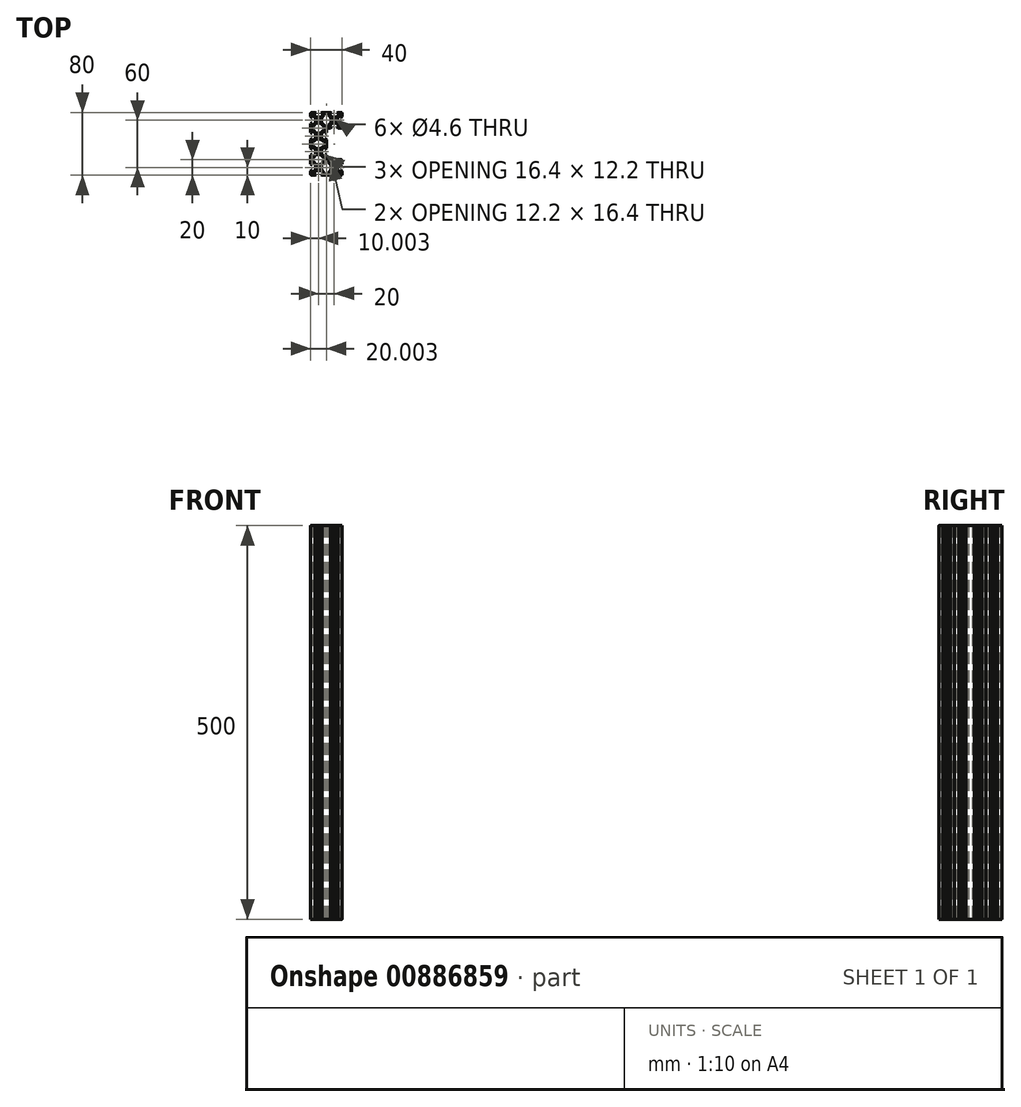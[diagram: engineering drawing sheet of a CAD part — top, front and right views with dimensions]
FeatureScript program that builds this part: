
annotation { "Feature Type Name" : "Feature", "Feature Type Description" : "" }
export const myFeature = defineFeature(function(context is Context, id is Id, definition is map)
    precondition{}
    {
        {
            var Q0;
            Q0=qCreatedBy(makeId("Top.planeOp"),FACE);
            var sketch = newSketch(context, id + "F0", { "sketchPlane" : qUnion([Q0])});
            skLineSegment(sketch, "E0", {"start": v(-12.56, -40) * mm, "end": v(-11.37, -38.82) * mm});
            skLineSegment(sketch, "E1", {"start": v(-11.37, -38.82) * mm, "end": v(-11.37, -38.2) * mm});
            skLineSegment(sketch, "E2", {"start": v(-11.37, -38.2) * mm, "end": v(-13.48, -38.2) * mm});
            skLineSegment(sketch, "E3", {"start": v(-13.48, -38.2) * mm, "end": v(-13.48, -36.56) * mm});
            skLineSegment(sketch, "E4", {"start": v(-13.48, -36.56) * mm, "end": v(-10.82, -33.9) * mm});
            skLineSegment(sketch, "E5", {"start": v(-10.82, -33.9) * mm, "end": v(-8.19, -33.9) * mm});
            skLineSegment(sketch, "E6", {"start": v(-8.19, -33.9) * mm, "end": v(-7.98, -33.7) * mm});
            skLineSegment(sketch, "E7", {"start": v(-7.98, -33.69) * mm, "end": v(-7.77, -33.9) * mm});
            skLineSegment(sketch, "E8", {"start": v(-7.77, -33.9) * mm, "end": v(-5.14, -33.9) * mm});
            skLineSegment(sketch, "E9", {"start": v(-5.14, -33.9) * mm, "end": v(-2.48, -36.56) * mm});
            skLineSegment(sketch, "E10", {"start": v(-2.48, -36.56) * mm, "end": v(-2.48, -38.2) * mm});
            skLineSegment(sketch, "E11", {"start": v(-2.48, -38.2) * mm, "end": v(-4.58, -38.2) * mm});
            skLineSegment(sketch, "E12", {"start": v(-4.58, -38.2) * mm, "end": v(-4.58, -38.82) * mm});
            skLineSegment(sketch, "E13", {"start": v(-4.58, -38.82) * mm, "end": v(-3.4, -40) * mm});
            skLineSegment(sketch, "E14", {"start": v(-3.4, -40) * mm, "end": v(7.44, -40) * mm});
            skLineSegment(sketch, "E15", {"start": v(7.44, -40) * mm, "end": v(8.63, -38.82) * mm});
            skLineSegment(sketch, "E16", {"start": v(8.63, -38.82) * mm, "end": v(8.63, -38.2) * mm});
            skLineSegment(sketch, "E17", {"start": v(8.63, -38.2) * mm, "end": v(6.52, -38.2) * mm});
            skLineSegment(sketch, "E18", {"start": v(6.52, -38.2) * mm, "end": v(6.52, -36.56) * mm});
            skLineSegment(sketch, "E19", {"start": v(6.52, -36.56) * mm, "end": v(9.18, -33.9) * mm});
            skLineSegment(sketch, "E20", {"start": v(9.18, -33.9) * mm, "end": v(11.81, -33.9) * mm});
            skLineSegment(sketch, "E21", {"start": v(11.81, -33.9) * mm, "end": v(12.02, -33.69) * mm});
            skLineSegment(sketch, "E22", {"start": v(12.02, -33.7) * mm, "end": v(12.23, -33.9) * mm});
            skLineSegment(sketch, "E23", {"start": v(12.23, -33.9) * mm, "end": v(14.86, -33.9) * mm});
            skLineSegment(sketch, "E24", {"start": v(14.86, -33.9) * mm, "end": v(17.52, -36.56) * mm});
            skLineSegment(sketch, "E25", {"start": v(17.52, -36.56) * mm, "end": v(17.52, -38.2) * mm});
            skLineSegment(sketch, "E26", {"start": v(17.52, -38.2) * mm, "end": v(15.42, -38.2) * mm});
            skLineSegment(sketch, "E27", {"start": v(15.42, -38.2) * mm, "end": v(15.42, -38.82) * mm});
            skLineSegment(sketch, "E28", {"start": v(15.42, -38.82) * mm, "end": v(16.6, -40) * mm});
            skLineSegment(sketch, "E29", {"start": v(16.6, -40) * mm, "end": v(20.52, -40) * mm});
            skLineSegment(sketch, "E30", {"start": v(22.02, -38.5) * mm, "end": v(22.02, -34.58) * mm});
            skLineSegment(sketch, "E31", {"start": v(22.02, -34.58) * mm, "end": v(20.84, -33.4) * mm});
            skLineSegment(sketch, "E32", {"start": v(20.84, -33.4) * mm, "end": v(20.22, -33.4) * mm});
            skLineSegment(sketch, "E33", {"start": v(20.22, -33.4) * mm, "end": v(20.22, -35.5) * mm});
            skLineSegment(sketch, "E34", {"start": v(20.22, -35.5) * mm, "end": v(18.58, -35.5) * mm});
            skLineSegment(sketch, "E35", {"start": v(18.58, -35.5) * mm, "end": v(15.92, -32.84) * mm});
            skLineSegment(sketch, "E36", {"start": v(15.92, -32.84) * mm, "end": v(15.92, -30.21) * mm});
            skLineSegment(sketch, "E37", {"start": v(15.92, -30.21) * mm, "end": v(15.71, -30) * mm});
            skLineSegment(sketch, "E38", {"start": v(15.71, -30) * mm, "end": v(15.92, -29.79) * mm});
            skLineSegment(sketch, "E39", {"start": v(15.92, -29.79) * mm, "end": v(15.92, -27.16) * mm});
            skLineSegment(sketch, "E40", {"start": v(15.92, -27.16) * mm, "end": v(18.58, -24.5) * mm});
            skLineSegment(sketch, "E41", {"start": v(18.58, -24.5) * mm, "end": v(20.22, -24.5) * mm});
            skLineSegment(sketch, "E42", {"start": v(20.22, -24.5) * mm, "end": v(20.22, -26.6) * mm});
            skLineSegment(sketch, "E43", {"start": v(20.22, -26.6) * mm, "end": v(20.84, -26.6) * mm});
            skLineSegment(sketch, "E44", {"start": v(20.84, -26.6) * mm, "end": v(22.02, -25.42) * mm});
            skLineSegment(sketch, "E45", {"start": v(22.02, -25.42) * mm, "end": v(22.02, -21.5) * mm});
            skLineSegment(sketch, "E46", {"start": v(20.52, -20) * mm, "end": v(16.6, -20) * mm});
            skLineSegment(sketch, "E47", {"start": v(16.6, -20) * mm, "end": v(15.42, -21.18) * mm});
            skLineSegment(sketch, "E48", {"start": v(15.42, -21.18) * mm, "end": v(15.42, -21.8) * mm});
            skLineSegment(sketch, "E49", {"start": v(15.42, -21.8) * mm, "end": v(17.52, -21.8) * mm});
            skLineSegment(sketch, "E50", {"start": v(17.52, -21.8) * mm, "end": v(17.52, -23.44) * mm});
            skLineSegment(sketch, "E51", {"start": v(17.52, -23.44) * mm, "end": v(14.86, -26.1) * mm});
            skLineSegment(sketch, "E52", {"start": v(14.86, -26.1) * mm, "end": v(12.23, -26.1) * mm});
            skLineSegment(sketch, "E53", {"start": v(12.23, -26.1) * mm, "end": v(12.02, -26.3) * mm});
            skLineSegment(sketch, "E54", {"start": v(12.02, -26.3) * mm, "end": v(11.81, -26.1) * mm});
            skLineSegment(sketch, "E55", {"start": v(11.81, -26.1) * mm, "end": v(9.18, -26.1) * mm});
            skLineSegment(sketch, "E56", {"start": v(9.18, -26.1) * mm, "end": v(6.52, -23.44) * mm});
            skLineSegment(sketch, "E57", {"start": v(6.52, -23.44) * mm, "end": v(6.52, -21.8) * mm});
            skLineSegment(sketch, "E58", {"start": v(-12.56, -40) * mm, "end": v(-16.48, -40) * mm});
            skLineSegment(sketch, "E59", {"start": v(6.52, -21.8) * mm, "end": v(8.63, -21.8) * mm});
            skLineSegment(sketch, "E60", {"start": v(-17.98, -38.5) * mm, "end": v(-17.98, -34.58) * mm});
            skLineSegment(sketch, "E61", {"start": v(8.63, -21.8) * mm, "end": v(8.63, -21.18) * mm});
            skLineSegment(sketch, "E62", {"start": v(-17.98, -34.58) * mm, "end": v(-16.8, -33.4) * mm});
            skLineSegment(sketch, "E63", {"start": v(8.63, -21.18) * mm, "end": v(7.44, -20) * mm});
            skLineSegment(sketch, "E64", {"start": v(-16.8, -33.4) * mm, "end": v(-16.18, -33.4) * mm});
            skLineSegment(sketch, "E65", {"start": v(7.44, -20) * mm, "end": v(2.02, -20) * mm});
            skLineSegment(sketch, "E66", {"start": v(-16.18, -33.4) * mm, "end": v(-16.18, -35.5) * mm});
            skLineSegment(sketch, "E67", {"start": v(2.02, -20) * mm, "end": v(2.02, -14.58) * mm});
            skLineSegment(sketch, "E68", {"start": v(-16.18, -35.5) * mm, "end": v(-14.54, -35.5) * mm});
            skLineSegment(sketch, "E69", {"start": v(2.02, -14.58) * mm, "end": v(0.84, -13.4) * mm});
            skLineSegment(sketch, "E70", {"start": v(-14.54, -35.5) * mm, "end": v(-11.88, -32.84) * mm});
            skLineSegment(sketch, "E71", {"start": v(0.84, -13.4) * mm, "end": v(0.22, -13.4) * mm});
            skLineSegment(sketch, "E72", {"start": v(-11.88, -32.84) * mm, "end": v(-11.88, -30.21) * mm});
            skLineSegment(sketch, "E73", {"start": v(0.22, -13.4) * mm, "end": v(0.22, -15.5) * mm});
            skLineSegment(sketch, "E74", {"start": v(-11.88, -30.21) * mm, "end": v(-11.67, -30) * mm});
            skLineSegment(sketch, "E75", {"start": v(0.22, -15.5) * mm, "end": v(-1.42, -15.5) * mm});
            skLineSegment(sketch, "E76", {"start": v(-11.67, -30) * mm, "end": v(-11.88, -29.79) * mm});
            skLineSegment(sketch, "E77", {"start": v(-1.42, -15.5) * mm, "end": v(-4.08, -12.84) * mm});
            skLineSegment(sketch, "E78", {"start": v(-11.88, -29.79) * mm, "end": v(-11.88, -27.16) * mm});
            skLineSegment(sketch, "E79", {"start": v(-4.08, -12.84) * mm, "end": v(-4.08, -10.21) * mm});
            skLineSegment(sketch, "E80", {"start": v(-11.88, -27.16) * mm, "end": v(-14.54, -24.5) * mm});
            skLineSegment(sketch, "E81", {"start": v(-4.08, -10.21) * mm, "end": v(-4.29, -10) * mm});
            skLineSegment(sketch, "E82", {"start": v(-14.54, -24.5) * mm, "end": v(-16.18, -24.5) * mm});
            skLineSegment(sketch, "E83", {"start": v(-4.29, -10) * mm, "end": v(-4.08, -9.8) * mm});
            skLineSegment(sketch, "E84", {"start": v(-16.18, -24.5) * mm, "end": v(-16.18, -26.6) * mm});
            skLineSegment(sketch, "E85", {"start": v(-4.08, -9.8) * mm, "end": v(-4.08, -7.16) * mm});
            skLineSegment(sketch, "E86", {"start": v(-16.18, -26.6) * mm, "end": v(-16.8, -26.6) * mm});
            skLineSegment(sketch, "E87", {"start": v(-4.08, -7.16) * mm, "end": v(-1.42, -4.5) * mm});
            skLineSegment(sketch, "E88", {"start": v(-16.8, -26.6) * mm, "end": v(-17.98, -25.42) * mm});
            skLineSegment(sketch, "E89", {"start": v(-1.42, -4.5) * mm, "end": v(0.22, -4.5) * mm});
            skLineSegment(sketch, "E90", {"start": v(-17.98, -25.42) * mm, "end": v(-17.98, -14.58) * mm});
            skLineSegment(sketch, "E91", {"start": v(0.22, -4.5) * mm, "end": v(0.22, -6.6) * mm});
            skLineSegment(sketch, "E92", {"start": v(-17.98, -14.58) * mm, "end": v(-16.8, -13.4) * mm});
            skLineSegment(sketch, "E93", {"start": v(0.22, -6.6) * mm, "end": v(0.84, -6.6) * mm});
            skLineSegment(sketch, "E94", {"start": v(-16.8, -13.4) * mm, "end": v(-16.18, -13.4) * mm});
            skLineSegment(sketch, "E95", {"start": v(0.84, -6.6) * mm, "end": v(2.02, -5.42) * mm});
            skLineSegment(sketch, "E96", {"start": v(-16.18, -13.4) * mm, "end": v(-16.18, -15.5) * mm});
            skLineSegment(sketch, "E97", {"start": v(2.02, -5.42) * mm, "end": v(2.02, 0) * mm});
            skLineSegment(sketch, "E98", {"start": v(-16.18, -15.5) * mm, "end": v(-14.54, -15.5) * mm});
            skLineSegment(sketch, "E99", {"start": v(-14.54, -15.5) * mm, "end": v(-11.88, -12.84) * mm});
            skLineSegment(sketch, "E100", {"start": v(-11.88, -12.84) * mm, "end": v(-11.88, -10.21) * mm});
            skLineSegment(sketch, "E101", {"start": v(-11.88, -10.21) * mm, "end": v(-11.67, -10) * mm});
            skLineSegment(sketch, "E102", {"start": v(-11.67, -10) * mm, "end": v(-11.88, -9.8) * mm});
            skLineSegment(sketch, "E103", {"start": v(-11.88, -9.8) * mm, "end": v(-11.88, -7.16) * mm});
            skLineSegment(sketch, "E104", {"start": v(-11.88, -7.16) * mm, "end": v(-14.54, -4.5) * mm});
            skLineSegment(sketch, "E105", {"start": v(-14.54, -4.5) * mm, "end": v(-16.18, -4.5) * mm});
            skLineSegment(sketch, "E106", {"start": v(-16.18, -4.5) * mm, "end": v(-16.18, -6.6) * mm});
            skLineSegment(sketch, "E107", {"start": v(-16.18, -6.6) * mm, "end": v(-16.8, -6.6) * mm});
            skLineSegment(sketch, "E108", {"start": v(-16.8, -6.6) * mm, "end": v(-17.98, -5.42) * mm});
            skLineSegment(sketch, "E109", {"start": v(-17.98, -5.42) * mm, "end": v(-17.98, 0) * mm});
            skLineSegment(sketch, "E110", {"start": v(-0.68, -38.2) * mm, "end": v(4.72, -38.2) * mm});
            skLineSegment(sketch, "E111", {"start": v(4.72, -38.2) * mm, "end": v(4.72, -36.24) * mm});
            skLineSegment(sketch, "E112", {"start": v(4.72, -36.24) * mm, "end": v(8.12, -32.84) * mm});
            skLineSegment(sketch, "E113", {"start": v(8.12, -32.84) * mm, "end": v(8.12, -27.16) * mm});
            skLineSegment(sketch, "E114", {"start": v(8.12, -27.16) * mm, "end": v(4.72, -23.76) * mm});
            skLineSegment(sketch, "E115", {"start": v(4.72, -23.76) * mm, "end": v(4.72, -21.8) * mm});
            skLineSegment(sketch, "E116", {"start": v(4.72, -21.8) * mm, "end": v(1.28, -21.8) * mm});
            skLineSegment(sketch, "E117", {"start": v(1.28, -21.8) * mm, "end": v(-4.08, -27.16) * mm});
            skLineSegment(sketch, "E118", {"start": v(-4.08, -27.16) * mm, "end": v(-4.08, -32.84) * mm});
            skLineSegment(sketch, "E119", {"start": v(-4.08, -32.84) * mm, "end": v(-0.68, -36.24) * mm});
            skLineSegment(sketch, "E120", {"start": v(-0.68, -36.24) * mm, "end": v(-0.68, -38.2) * mm});
            skLineSegment(sketch, "E121", {"start": v(-10.82, -26.1) * mm, "end": v(-5.14, -26.1) * mm});
            skLineSegment(sketch, "E122", {"start": v(-5.14, -26.1) * mm, "end": v(0.22, -20.74) * mm});
            skLineSegment(sketch, "E123", {"start": v(0.22, -20.74) * mm, "end": v(0.22, -17.3) * mm});
            skLineSegment(sketch, "E124", {"start": v(0.22, -17.3) * mm, "end": v(-1.74, -17.3) * mm});
            skLineSegment(sketch, "E125", {"start": v(-1.74, -17.3) * mm, "end": v(-5.14, -13.9) * mm});
            skLineSegment(sketch, "E126", {"start": v(-5.14, -13.9) * mm, "end": v(-10.82, -13.9) * mm});
            skLineSegment(sketch, "E127", {"start": v(-10.82, -13.9) * mm, "end": v(-14.22, -17.3) * mm});
            skLineSegment(sketch, "E128", {"start": v(-14.22, -17.3) * mm, "end": v(-16.18, -17.3) * mm});
            skLineSegment(sketch, "E129", {"start": v(-16.18, -17.3) * mm, "end": v(-16.18, -22.7) * mm});
            skLineSegment(sketch, "E130", {"start": v(-16.18, -22.7) * mm, "end": v(-14.22, -22.7) * mm});
            skLineSegment(sketch, "E131", {"start": v(-14.22, -22.7) * mm, "end": v(-10.82, -26.1) * mm});
            skLineSegment(sketch, "E132", {"start": v(-16.18, 0) * mm, "end": v(-16.18, -2.7) * mm});
            skLineSegment(sketch, "E133", {"start": v(-16.18, -2.7) * mm, "end": v(-14.22, -2.7) * mm});
            skLineSegment(sketch, "E134", {"start": v(-14.22, -2.7) * mm, "end": v(-10.82, -6.1) * mm});
            skLineSegment(sketch, "E135", {"start": v(-10.82, -6.1) * mm, "end": v(-5.14, -6.1) * mm});
            skLineSegment(sketch, "E136", {"start": v(-5.14, -6.1) * mm, "end": v(-1.74, -2.7) * mm});
            skLineSegment(sketch, "E137", {"start": v(-1.74, -2.7) * mm, "end": v(0.22, -2.7) * mm});
            skLineSegment(sketch, "E138", {"start": v(0.22, -2.7) * mm, "end": v(0.22, 0) * mm});
            skCircle(sketch, "E139", {"center": v(-7.98, -10) * mm, "radius": 2.3 * mm});
            skPoint(sketch, "E139.first.point", {"position": v(-9.64, -11.59) * mm});
            skPoint(sketch, "E139.second.point", {"position": v(-5.77, -10.63) * mm});
            skPoint(sketch, "E139.third.point", {"position": v(-6.97, -7.93) * mm});
            skCircle(sketch, "E140", {"center": v(-7.98, -30) * mm, "radius": 2.3 * mm});
            skPoint(sketch, "E140.first.point", {"position": v(-10.02, -31.05) * mm});
            skPoint(sketch, "E140.second.point", {"position": v(-6.08, -31.3) * mm});
            skPoint(sketch, "E140.third.point", {"position": v(-6.51, -28.23) * mm});
            skCircle(sketch, "E141", {"center": v(12.02, -30) * mm, "radius": 2.3 * mm});
            skPoint(sketch, "E141.first.point", {"position": v(9.96, -31) * mm});
            skPoint(sketch, "E141.second.point", {"position": v(14.22, -30.67) * mm});
            skPoint(sketch, "E141.third.point", {"position": v(13.22, -28.04) * mm});
            skLineSegment(sketch, "E142", {"start": v(-28.08, 0) * mm, "end": v(32.1, 0) * mm, "construction": true});
            skLineSegment(sketch, "E143.MirrorCS", {"start": v(-8.19, 33.9) * mm, "end": v(-7.98, 33.69) * mm});
            skLineSegment(sketch, "E144.MirrorCS", {"start": v(-11.67, 10) * mm, "end": v(-11.88, 9.8) * mm});
            skLineSegment(sketch, "E145.MirrorCS", {"start": v(-7.98, 33.69) * mm, "end": v(-7.77, 33.9) * mm});
            skLineSegment(sketch, "E146.MirrorCS", {"start": v(-11.88, 10.2) * mm, "end": v(-11.67, 10) * mm});
            skLineSegment(sketch, "E147.MirrorCS", {"start": v(-4.29, 10) * mm, "end": v(-4.08, 9.8) * mm});
            skLineSegment(sketch, "E148.MirrorCS", {"start": v(17.52, 38.2) * mm, "end": v(15.42, 38.2) * mm});
            skLineSegment(sketch, "E149.MirrorCS", {"start": v(-16.18, 4.5) * mm, "end": v(-16.18, 6.6) * mm});
            skLineSegment(sketch, "E150.MirrorCS", {"start": v(-11.88, 30.2) * mm, "end": v(-11.67, 30) * mm});
            skLineSegment(sketch, "E151.MirrorCS", {"start": v(-14.54, 24.5) * mm, "end": v(-16.18, 24.5) * mm});
            skLineSegment(sketch, "E152.MirrorCS", {"start": v(-16.18, 15.5) * mm, "end": v(-14.54, 15.5) * mm});
            skLineSegment(sketch, "E153.MirrorCS", {"start": v(-16.18, 22.7) * mm, "end": v(-14.22, 22.7) * mm});
            skLineSegment(sketch, "E154.MirrorCS", {"start": v(6.52, 38.2) * mm, "end": v(6.52, 36.56) * mm});
            skLineSegment(sketch, "E155.MirrorCS", {"start": v(20.22, 35.5) * mm, "end": v(18.58, 35.5) * mm});
            skLineSegment(sketch, "E156.MirrorCS", {"start": v(17.52, 21.8) * mm, "end": v(17.52, 23.44) * mm});
            skLineSegment(sketch, "E157.MirrorCS", {"start": v(4.72, 23.76) * mm, "end": v(4.72, 21.8) * mm});
            skLineSegment(sketch, "E158.MirrorCS", {"start": v(-16.18, 33.4) * mm, "end": v(-16.18, 35.5) * mm});
            skLineSegment(sketch, "E159.MirrorCS", {"start": v(-1.74, 2.7) * mm, "end": v(0.22, 2.7) * mm});
            skLineSegment(sketch, "E160.MirrorCS", {"start": v(6.52, 23.44) * mm, "end": v(6.52, 21.8) * mm});
            skLineSegment(sketch, "E161.MirrorCS", {"start": v(0.22, 13.4) * mm, "end": v(0.22, 15.5) * mm});
            skLineSegment(sketch, "E162.MirrorCS", {"start": v(-1.42, 4.5) * mm, "end": v(0.22, 4.5) * mm});
            skLineSegment(sketch, "E163.MirrorCS", {"start": v(-14.54, 4.5) * mm, "end": v(-16.18, 4.5) * mm});
            skLineSegment(sketch, "E164.MirrorCS", {"start": v(17.52, 36.56) * mm, "end": v(17.52, 38.2) * mm});
            skLineSegment(sketch, "E165.MirrorCS", {"start": v(18.58, 24.5) * mm, "end": v(20.22, 24.5) * mm});
            skLineSegment(sketch, "E166.MirrorCS", {"start": v(-4.08, 10.21) * mm, "end": v(-4.29, 10) * mm});
            skLineSegment(sketch, "E167.MirrorCS", {"start": v(-16.8, 26.6) * mm, "end": v(-17.98, 25.42) * mm});
            skLineSegment(sketch, "E168.MirrorCS", {"start": v(-4.58, 38.2) * mm, "end": v(-4.58, 38.82) * mm});
            skLineSegment(sketch, "E169.MirrorCS", {"start": v(-2.48, 38.2) * mm, "end": v(-4.58, 38.2) * mm});
            skLineSegment(sketch, "E170.MirrorCS", {"start": v(20.84, 33.4) * mm, "end": v(20.22, 33.4) * mm});
            skLineSegment(sketch, "E171.MirrorCS", {"start": v(-16.8, 33.4) * mm, "end": v(-16.18, 33.4) * mm});
            skLineSegment(sketch, "E172.MirrorCS", {"start": v(15.42, 21.18) * mm, "end": v(15.42, 21.8) * mm});
            skLineSegment(sketch, "E173.MirrorCS", {"start": v(-13.48, 38.2) * mm, "end": v(-13.48, 36.56) * mm});
            skLineSegment(sketch, "E174.MirrorCS", {"start": v(-11.37, 38.82) * mm, "end": v(-11.37, 38.2) * mm});
            skLineSegment(sketch, "E175.MirrorCS", {"start": v(-12.56, 40) * mm, "end": v(-11.37, 38.82) * mm});
            skLineSegment(sketch, "E176.MirrorCS", {"start": v(0.84, 13.4) * mm, "end": v(0.22, 13.4) * mm});
            skLineSegment(sketch, "E177.MirrorCS", {"start": v(7.44, 40) * mm, "end": v(8.63, 38.82) * mm});
            skLineSegment(sketch, "E178.MirrorCS", {"start": v(-4.58, 38.82) * mm, "end": v(-3.4, 40) * mm});
            skLineSegment(sketch, "E179.MirrorCS", {"start": v(-16.18, 13.4) * mm, "end": v(-16.18, 15.5) * mm});
            skLineSegment(sketch, "E180.MirrorCS", {"start": v(-14.22, 17.3) * mm, "end": v(-16.18, 17.3) * mm});
            skLineSegment(sketch, "E181.MirrorCS", {"start": v(-16.18, 26.6) * mm, "end": v(-16.8, 26.6) * mm});
            skLineSegment(sketch, "E182.MirrorCS", {"start": v(4.72, 38.2) * mm, "end": v(4.72, 36.24) * mm});
            skLineSegment(sketch, "E183.MirrorCS", {"start": v(0.84, 6.6) * mm, "end": v(2.02, 5.42) * mm});
            skLineSegment(sketch, "E184.MirrorCS", {"start": v(22.02, 34.58) * mm, "end": v(20.84, 33.4) * mm});
            skLineSegment(sketch, "E185.MirrorCS", {"start": v(12.02, 26.3) * mm, "end": v(11.81, 26.1) * mm});
            skLineSegment(sketch, "E186.MirrorCS", {"start": v(15.71, 30) * mm, "end": v(15.92, 29.79) * mm});
            skLineSegment(sketch, "E187.MirrorCS", {"start": v(8.63, 21.18) * mm, "end": v(7.44, 20) * mm});
            skLineSegment(sketch, "E188.MirrorCS", {"start": v(-11.67, 30) * mm, "end": v(-11.88, 29.79) * mm});
            skLineSegment(sketch, "E189.MirrorCS", {"start": v(-16.8, 6.6) * mm, "end": v(-17.98, 5.42) * mm});
            skLineSegment(sketch, "E190.MirrorCS", {"start": v(20.84, 26.6) * mm, "end": v(22.02, 25.42) * mm});
            skLineSegment(sketch, "E191.MirrorCS", {"start": v(8.63, 21.8) * mm, "end": v(8.63, 21.18) * mm});
            skLineSegment(sketch, "E192.MirrorCS", {"start": v(-16.18, 35.5) * mm, "end": v(-14.54, 35.5) * mm});
            skLineSegment(sketch, "E193.MirrorCS", {"start": v(0.22, 4.5) * mm, "end": v(0.22, 6.6) * mm});
            skLineSegment(sketch, "E194.MirrorCS", {"start": v(-16.18, 6.6) * mm, "end": v(-16.8, 6.6) * mm});
            skLineSegment(sketch, "E195.MirrorCS", {"start": v(20.22, 26.6) * mm, "end": v(20.84, 26.6) * mm});
            skLineSegment(sketch, "E196.MirrorCS", {"start": v(8.63, 38.2) * mm, "end": v(6.52, 38.2) * mm});
            skLineSegment(sketch, "E197.MirrorCS", {"start": v(15.42, 21.8) * mm, "end": v(17.52, 21.8) * mm});
            skLineSegment(sketch, "E198.MirrorCS", {"start": v(20.22, 33.4) * mm, "end": v(20.22, 35.5) * mm});
            skLineSegment(sketch, "E199.MirrorCS", {"start": v(-0.68, 36.24) * mm, "end": v(-0.68, 38.2) * mm});
            skLineSegment(sketch, "E200.MirrorCS", {"start": v(-2.48, 36.56) * mm, "end": v(-2.48, 38.2) * mm});
            skLineSegment(sketch, "E201.MirrorCS", {"start": v(8.63, 38.82) * mm, "end": v(8.63, 38.2) * mm});
            skLineSegment(sketch, "E202.MirrorCS", {"start": v(-11.37, 38.2) * mm, "end": v(-13.48, 38.2) * mm});
            skLineSegment(sketch, "E203.MirrorCS", {"start": v(12.02, 33.69) * mm, "end": v(12.23, 33.9) * mm});
            skLineSegment(sketch, "E204.MirrorCS", {"start": v(16.6, 20) * mm, "end": v(15.42, 21.18) * mm});
            skLineSegment(sketch, "E205.MirrorCS", {"start": v(-16.18, 2.7) * mm, "end": v(-14.22, 2.7) * mm});
            skLineSegment(sketch, "E206.MirrorCS", {"start": v(12.23, 26.1) * mm, "end": v(12.02, 26.3) * mm});
            skLineSegment(sketch, "E207.MirrorCS", {"start": v(-17.98, 14.58) * mm, "end": v(-16.8, 13.4) * mm});
            skLineSegment(sketch, "E208.MirrorCS", {"start": v(15.42, 38.82) * mm, "end": v(16.6, 40) * mm});
            skLineSegment(sketch, "E209.MirrorCS", {"start": v(20.22, 24.5) * mm, "end": v(20.22, 26.6) * mm});
            skLineSegment(sketch, "E210.MirrorCS", {"start": v(6.52, 21.8) * mm, "end": v(8.63, 21.8) * mm});
            skLineSegment(sketch, "E211.MirrorCS", {"start": v(0.22, 15.5) * mm, "end": v(-1.42, 15.5) * mm});
            skLineSegment(sketch, "E212.MirrorCS", {"start": v(-16.8, 13.4) * mm, "end": v(-16.18, 13.4) * mm});
            skLineSegment(sketch, "E213.MirrorCS", {"start": v(11.81, 33.9) * mm, "end": v(12.02, 33.69) * mm});
            skLineSegment(sketch, "E214.MirrorCS", {"start": v(15.92, 30.21) * mm, "end": v(15.71, 30) * mm});
            skLineSegment(sketch, "E215.MirrorCS", {"start": v(2.02, 14.58) * mm, "end": v(0.84, 13.4) * mm});
            skLineSegment(sketch, "E216.MirrorCS", {"start": v(-17.98, 34.58) * mm, "end": v(-16.8, 33.4) * mm});
            skLineSegment(sketch, "E217.MirrorCS", {"start": v(0.22, 17.3) * mm, "end": v(-1.74, 17.3) * mm});
            skLineSegment(sketch, "E218.MirrorCS", {"start": v(-16.18, 24.5) * mm, "end": v(-16.18, 26.6) * mm});
            skLineSegment(sketch, "E219.MirrorCS", {"start": v(0.22, 6.6) * mm, "end": v(0.84, 6.6) * mm});
            skLineSegment(sketch, "E220.MirrorCS", {"start": v(15.42, 38.2) * mm, "end": v(15.42, 38.82) * mm});
            skLineSegment(sketch, "E221.MirrorCS", {"start": v(-17.98, 25.42) * mm, "end": v(-17.98, 14.58) * mm});
            skLineSegment(sketch, "E222.MirrorCS", {"start": v(-12.56, 40) * mm, "end": v(-16.48, 40) * mm});
            skLineSegment(sketch, "E223.MirrorCS", {"start": v(0.22, 2.7) * mm, "end": v(0.22, 0) * mm});
            skLineSegment(sketch, "E224.MirrorCS", {"start": v(-5.14, 26.1) * mm, "end": v(0.22, 20.74) * mm});
            skPoint(sketch, "E225.MirrorP", {"position": v(13.22, 28.04) * mm});
            skLineSegment(sketch, "E226.MirrorCS", {"start": v(2.02, 20) * mm, "end": v(2.02, 14.58) * mm});
            skLineSegment(sketch, "E227.MirrorCS", {"start": v(17.52, 23.44) * mm, "end": v(14.86, 26.1) * mm});
            skLineSegment(sketch, "E228.MirrorCS", {"start": v(8.12, 27.16) * mm, "end": v(4.72, 23.76) * mm});
            skLineSegment(sketch, "E229.MirrorCS", {"start": v(18.58, 35.5) * mm, "end": v(15.92, 32.84) * mm});
            skLineSegment(sketch, "E230.MirrorCS", {"start": v(6.52, 36.56) * mm, "end": v(9.18, 33.9) * mm});
            skLineSegment(sketch, "E231.MirrorCS", {"start": v(-14.22, 22.7) * mm, "end": v(-10.82, 26.1) * mm});
            skLineSegment(sketch, "E232.MirrorCS", {"start": v(-14.54, 15.5) * mm, "end": v(-11.88, 12.84) * mm});
            skPoint(sketch, "E233.MirrorP", {"position": v(14.22, 30.67) * mm});
            skPoint(sketch, "E234.MirrorP", {"position": v(-5.77, 10.63) * mm});
            skLineSegment(sketch, "E235.MirrorCS", {"start": v(-10.82, 26.1) * mm, "end": v(-5.14, 26.1) * mm});
            skPoint(sketch, "E236.MirrorP", {"position": v(-9.64, 11.59) * mm});
            skLineSegment(sketch, "E237.MirrorCS", {"start": v(7.44, 20) * mm, "end": v(2.02, 20) * mm});
            skLineSegment(sketch, "E238.MirrorCS", {"start": v(-5.14, 6.1) * mm, "end": v(-1.74, 2.7) * mm});
            skLineSegment(sketch, "E239.MirrorCS", {"start": v(-11.88, 32.84) * mm, "end": v(-11.88, 30.21) * mm});
            skLineSegment(sketch, "E240.MirrorCS", {"start": v(15.92, 27.16) * mm, "end": v(18.58, 24.5) * mm});
            skLineSegment(sketch, "E241.MirrorCS", {"start": v(14.86, 33.9) * mm, "end": v(17.52, 36.56) * mm});
            skLineSegment(sketch, "E242.MirrorCS", {"start": v(-5.14, 33.9) * mm, "end": v(-2.48, 36.56) * mm});
            skLineSegment(sketch, "E243.MirrorCS", {"start": v(11.81, 26.1) * mm, "end": v(9.18, 26.1) * mm});
            skLineSegment(sketch, "E244.MirrorCS", {"start": v(-4.08, 7.16) * mm, "end": v(-1.42, 4.5) * mm});
            skLineSegment(sketch, "E245.MirrorCS", {"start": v(-11.88, 9.8) * mm, "end": v(-11.88, 7.16) * mm});
            skLineSegment(sketch, "E246.MirrorCS", {"start": v(12.23, 33.9) * mm, "end": v(14.86, 33.9) * mm});
            skLineSegment(sketch, "E247.MirrorCS", {"start": v(15.92, 29.79) * mm, "end": v(15.92, 27.16) * mm});
            skLineSegment(sketch, "E248.MirrorCS", {"start": v(-3.4, 40) * mm, "end": v(7.44, 40) * mm});
            skLineSegment(sketch, "E249.MirrorCS", {"start": v(-4.08, 12.84) * mm, "end": v(-4.08, 10.21) * mm});
            skLineSegment(sketch, "E250.MirrorCS", {"start": v(-4.08, 27.16) * mm, "end": v(-4.08, 32.84) * mm});
            skLineSegment(sketch, "E251.MirrorCS", {"start": v(-14.22, 2.7) * mm, "end": v(-10.82, 6.1) * mm});
            skLineSegment(sketch, "E252.MirrorCS", {"start": v(-10.82, 13.9) * mm, "end": v(-14.22, 17.3) * mm});
            skLineSegment(sketch, "E253.MirrorCS", {"start": v(-14.54, 35.5) * mm, "end": v(-11.88, 32.84) * mm});
            skLineSegment(sketch, "E254.MirrorCS", {"start": v(-5.14, 13.9) * mm, "end": v(-10.82, 13.9) * mm});
            skLineSegment(sketch, "E255.MirrorCS", {"start": v(1.28, 21.8) * mm, "end": v(-4.08, 27.16) * mm});
            skPoint(sketch, "E256.MirrorP", {"position": v(-6.08, 31.3) * mm});
            skPoint(sketch, "E257.MirrorP", {"position": v(-6.97, 7.93) * mm});
            skLineSegment(sketch, "E258.MirrorCS", {"start": v(-11.88, 12.84) * mm, "end": v(-11.88, 10.21) * mm});
            skLineSegment(sketch, "E259.MirrorCS", {"start": v(-16.18, 0) * mm, "end": v(-16.18, 2.7) * mm});
            skLineSegment(sketch, "E260.MirrorCS", {"start": v(-1.74, 17.3) * mm, "end": v(-5.14, 13.9) * mm});
            skLineSegment(sketch, "E261.MirrorCS", {"start": v(16.6, 40) * mm, "end": v(20.52, 40) * mm});
            skLineSegment(sketch, "E262.MirrorCS", {"start": v(22.02, 25.42) * mm, "end": v(22.02, 21.5) * mm});
            skLineSegment(sketch, "E263.MirrorCS", {"start": v(0.22, 20.74) * mm, "end": v(0.22, 17.3) * mm});
            skLineSegment(sketch, "E264.MirrorCS", {"start": v(8.12, 32.84) * mm, "end": v(8.12, 27.16) * mm});
            skLineSegment(sketch, "E265.MirrorCS", {"start": v(2.02, 5.42) * mm, "end": v(2.02, 0) * mm});
            skLineSegment(sketch, "E266.MirrorCS", {"start": v(-16.18, 17.3) * mm, "end": v(-16.18, 22.7) * mm});
            skPoint(sketch, "E267.MirrorP", {"position": v(9.96, 31) * mm});
            skLineSegment(sketch, "E268.MirrorCS", {"start": v(9.18, 26.1) * mm, "end": v(6.52, 23.44) * mm});
            skLineSegment(sketch, "E269.MirrorCS", {"start": v(-11.88, 7.16) * mm, "end": v(-14.54, 4.5) * mm});
            skLineSegment(sketch, "E270.MirrorCS", {"start": v(-4.08, 32.84) * mm, "end": v(-0.68, 36.24) * mm});
            skLineSegment(sketch, "E271.MirrorCS", {"start": v(-10.82, 6.1) * mm, "end": v(-5.14, 6.1) * mm});
            skLineSegment(sketch, "E272.MirrorCS", {"start": v(-7.77, 33.9) * mm, "end": v(-5.14, 33.9) * mm});
            skLineSegment(sketch, "E273.MirrorCS", {"start": v(-10.82, 33.9) * mm, "end": v(-8.19, 33.9) * mm});
            skLineSegment(sketch, "E274.MirrorCS", {"start": v(-13.48, 36.56) * mm, "end": v(-10.82, 33.9) * mm});
            skLineSegment(sketch, "E275.MirrorCS", {"start": v(-11.88, 27.16) * mm, "end": v(-14.54, 24.5) * mm});
            skLineSegment(sketch, "E276.MirrorCS", {"start": v(4.72, 36.24) * mm, "end": v(8.12, 32.84) * mm});
            skPoint(sketch, "E277.MirrorP", {"position": v(-6.51, 28.23) * mm});
            skLineSegment(sketch, "E278.MirrorCS", {"start": v(-11.88, 29.79) * mm, "end": v(-11.88, 27.16) * mm});
            skLineSegment(sketch, "E279.MirrorCS", {"start": v(20.52, 20) * mm, "end": v(16.6, 20) * mm});
            skLineSegment(sketch, "E280.MirrorCS", {"start": v(-17.98, 38.5) * mm, "end": v(-17.98, 34.58) * mm});
            skCircle(sketch, "E281.MirrorC", {"center": v(-7.98, 30) * mm, "radius": 2.3 * mm});
            skLineSegment(sketch, "E282.MirrorCS", {"start": v(4.72, 21.8) * mm, "end": v(1.28, 21.8) * mm});
            skLineSegment(sketch, "E283.MirrorCS", {"start": v(-17.98, 5.42) * mm, "end": v(-17.98, 0) * mm});
            skLineSegment(sketch, "E284.MirrorCS", {"start": v(9.18, 33.9) * mm, "end": v(11.81, 33.9) * mm});
            skLineSegment(sketch, "E285.MirrorCS", {"start": v(15.92, 32.84) * mm, "end": v(15.92, 30.21) * mm});
            skLineSegment(sketch, "E286.MirrorCS", {"start": v(14.86, 26.1) * mm, "end": v(12.23, 26.1) * mm});
            skCircle(sketch, "E287.MirrorC", {"center": v(-7.98, 10) * mm, "radius": 2.3 * mm});
            skLineSegment(sketch, "E288.MirrorCS", {"start": v(-4.08, 9.8) * mm, "end": v(-4.08, 7.16) * mm});
            skLineSegment(sketch, "E289.MirrorCS", {"start": v(-0.68, 38.2) * mm, "end": v(4.72, 38.2) * mm});
            skLineSegment(sketch, "E290.MirrorCS", {"start": v(22.02, 38.5) * mm, "end": v(22.02, 34.58) * mm});
            skCircle(sketch, "E291.MirrorC", {"center": v(12.02, 30) * mm, "radius": 2.3 * mm});
            skLineSegment(sketch, "E292.MirrorCS", {"start": v(-1.42, 15.5) * mm, "end": v(-4.08, 12.84) * mm});
            skPoint(sketch, "E293.MirrorP", {"position": v(-10.02, 31.05) * mm});
            skPoint(sketch, "E294.visualSharp", {"position": v(-17.98, -40) * mm});
            skArc(sketch, "E294.filletArc", {"start": v(-17.98, -38.5) * mm, "mid": v(-17.54, -39.56) * mm, "end": v(-16.48, -40) * mm});
            skPoint(sketch, "E295.visualSharp", {"position": v(22.02, -40) * mm});
            skArc(sketch, "E295.filletArc", {"start": v(20.52, -40) * mm, "mid": v(21.58, -39.56) * mm, "end": v(22.02, -38.5) * mm});
            skPoint(sketch, "E296.visualSharp", {"position": v(22.02, -20) * mm});
            skArc(sketch, "E296.filletArc", {"start": v(22.02, -21.5) * mm, "mid": v(21.58, -20.44) * mm, "end": v(20.52, -20) * mm});
            skPoint(sketch, "E297.visualSharp", {"position": v(-17.98, 40) * mm});
            skArc(sketch, "E297.filletArc", {"start": v(-16.48, 40) * mm, "mid": v(-17.54, 39.56) * mm, "end": v(-17.98, 38.5) * mm});
            skPoint(sketch, "E298.visualSharp", {"position": v(22.02, 40) * mm});
            skArc(sketch, "E298.filletArc", {"start": v(22.02, 38.5) * mm, "mid": v(21.58, 39.56) * mm, "end": v(20.52, 40) * mm});
            skPoint(sketch, "E299.visualSharp", {"position": v(22.02, 20) * mm});
            skArc(sketch, "E299.filletArc", {"start": v(20.52, 20) * mm, "mid": v(21.58, 20.44) * mm, "end": v(22.02, 21.5) * mm});
            skSolve(sketch);
        }
        {
            var Q0;
            Q0=qSketchRegion(id+"F0",true);
            extrude(context, id + "F1", {"entities" : qUnion([Q0]), "depth" : 500 * mm});
        }
    });
